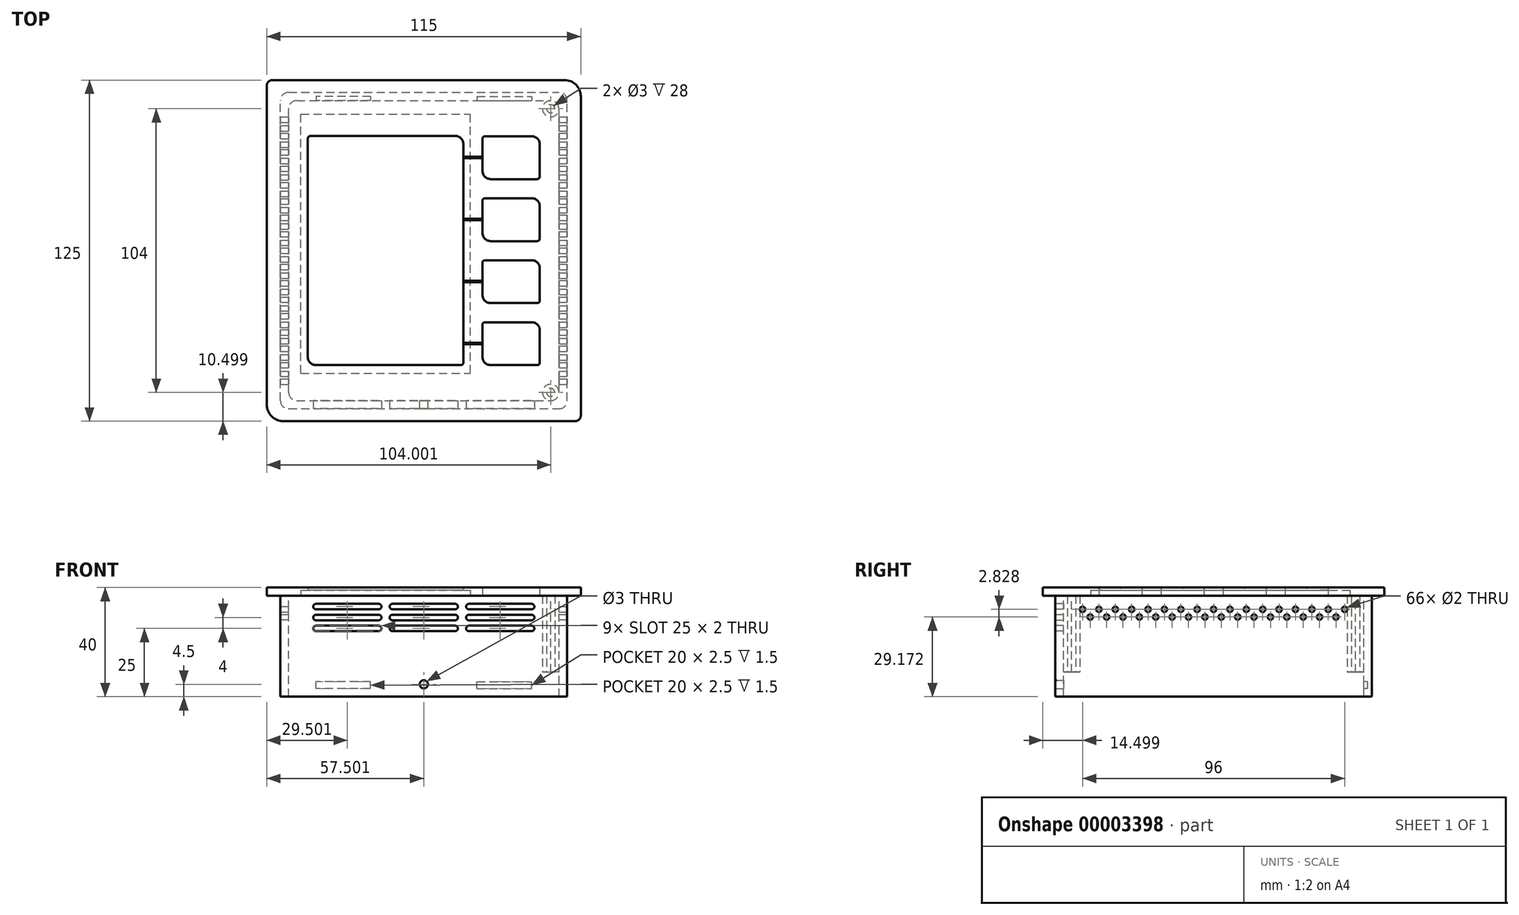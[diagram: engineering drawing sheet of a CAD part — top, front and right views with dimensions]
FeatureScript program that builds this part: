
annotation { "Feature Type Name" : "Feature", "Feature Type Description" : "" }
export const myFeature = defineFeature(function(context is Context, id is Id, definition is map)
    precondition{}
    {
        {
            var Q0;
            Q0=qCreatedBy(makeId("Top.planeOp"),FACE);
            var sketch = newSketch(context, id + "F0", { "sketchPlane" : qUnion([Q0])});
            skLineSegment(sketch, "E0.bottom", {"start": v(-65.66, 62.93) * mm, "end": v(49.34, 62.93) * mm});
            skLineSegment(sketch, "E0.top", {"start": v(-65.66, -62.07) * mm, "end": v(49.34, -62.07) * mm});
            skLineSegment(sketch, "E0.left", {"start": v(-65.66, 62.93) * mm, "end": v(-65.66, -62.07) * mm});
            skLineSegment(sketch, "E0.right", {"start": v(49.34, 62.93) * mm, "end": v(49.34, -62.07) * mm});
            skLineSegment(sketch, "E1.bottom", {"start": v(-50.66, 42.43) * mm, "end": v(6.34, 42.43) * mm});
            skLineSegment(sketch, "E1.top", {"start": v(-50.66, -41.57) * mm, "end": v(6.34, -41.57) * mm});
            skLineSegment(sketch, "E1.left", {"start": v(-50.66, 42.43) * mm, "end": v(-50.66, -41.57) * mm});
            skLineSegment(sketch, "E1.right", {"start": v(6.34, 42.43) * mm, "end": v(6.34, -41.57) * mm});
            skLineSegment(sketch, "E2", {"start": v(13.34, 42.43) * mm, "end": v(13.34, -41.57) * mm, "construction": true});
            skLineSegment(sketch, "E3", {"start": v(34.34, 42.43) * mm, "end": v(34.34, -41.57) * mm, "construction": true});
            skLineSegment(sketch, "E4.bottom", {"start": v(13.34, -41.57) * mm, "end": v(34.34, -41.57) * mm});
            skLineSegment(sketch, "E4.top", {"start": v(13.34, -25.84) * mm, "end": v(34.34, -25.84) * mm});
            skLineSegment(sketch, "E4.left", {"start": v(13.34, -41.57) * mm, "end": v(13.34, -25.84) * mm});
            skLineSegment(sketch, "E4.right", {"start": v(34.34, -41.57) * mm, "end": v(34.34, -25.84) * mm});
            skLineSegment(sketch, "E5.bottom", {"start": v(13.34, -18.84) * mm, "end": v(34.34, -18.84) * mm});
            skLineSegment(sketch, "E5.top", {"start": v(13.34, -3.11) * mm, "end": v(34.34, -3.11) * mm});
            skLineSegment(sketch, "E5.left", {"start": v(13.34, -18.84) * mm, "end": v(13.34, -3.11) * mm});
            skLineSegment(sketch, "E5.right", {"start": v(34.34, -18.84) * mm, "end": v(34.34, -3.11) * mm});
            skLineSegment(sketch, "E6.bottom", {"start": v(13.34, 3.89) * mm, "end": v(34.34, 3.89) * mm});
            skLineSegment(sketch, "E6.top", {"start": v(13.34, 19.62) * mm, "end": v(34.34, 19.62) * mm});
            skLineSegment(sketch, "E6.left", {"start": v(13.34, 3.89) * mm, "end": v(13.34, 19.62) * mm});
            skLineSegment(sketch, "E6.right", {"start": v(34.34, 3.89) * mm, "end": v(34.34, 19.62) * mm});
            skLineSegment(sketch, "E7.bottom", {"start": v(13.34, 26.62) * mm, "end": v(34.34, 26.62) * mm});
            skLineSegment(sketch, "E7.top", {"start": v(13.34, 42.35) * mm, "end": v(34.34, 42.35) * mm});
            skLineSegment(sketch, "E7.left", {"start": v(13.34, 26.62) * mm, "end": v(13.34, 42.35) * mm});
            skLineSegment(sketch, "E7.right", {"start": v(34.34, 26.62) * mm, "end": v(34.34, 42.35) * mm});
            skSolve(sketch);
        }
        {
            var Q0;
            Q0=makeQuery(id+"F0.imprint","IMPRINT",FACE,{"disambiguationData":[TD([[makeQuery(id+"F0.imprint","IMPRINT",EDGE,{"derivedFrom":sQuery(id+"F0.wireOp",EDGE,"E0.bottom")}),-1.0]])]});
            extrude(context, id + "F1", {"entities" : qUnion([Q0]), "depth" : 3 * mm});
        }
        {
            var Q0;
            Q0=makeQuery(id+"F1.opExtrude","SWEPT_EDGE",EDGE,{"disambiguationData":[OSD([sQuery(id+"F0.wireOp",EDGE,"E0.bottom"),sQuery(id+"F0.wireOp",EDGE,"E0.right")])]});
            var Q1;
            Q1=makeQuery(id+"F1.opExtrude","SWEPT_EDGE",EDGE,{"disambiguationData":[OSD([sQuery(id+"F0.wireOp",EDGE,"E0.top"),sQuery(id+"F0.wireOp",EDGE,"E0.left")])]});
            fillet(context, id + "F2", {"entities" : qUnion([Q0, Q1]), "radius" : 6 * mm, "tangentPropagation" : true, "allowEdgeOverflow" : false});
        }
        {
            var Q0;
            Q0=makeQuery(id+"F1.opExtrude","SWEPT_EDGE",EDGE,{"disambiguationData":[OSD([sQuery(id+"F0.wireOp",EDGE,"E7.top"),sQuery(id+"F0.wireOp",EDGE,"E7.right")])]});
            var Q1;
            Q1=makeQuery(id+"F1.opExtrude","SWEPT_EDGE",EDGE,{"disambiguationData":[OSD([sQuery(id+"F0.wireOp",EDGE,"E6.top"),sQuery(id+"F0.wireOp",EDGE,"E6.right")])]});
            var Q2;
            Q2=makeQuery(id+"F1.opExtrude","SWEPT_EDGE",EDGE,{"disambiguationData":[OSD([sQuery(id+"F0.wireOp",EDGE,"E5.top"),sQuery(id+"F0.wireOp",EDGE,"E5.right")])]});
            var Q3;
            Q3=makeQuery(id+"F1.opExtrude","SWEPT_EDGE",EDGE,{"disambiguationData":[OSD([sQuery(id+"F0.wireOp",EDGE,"E4.top"),sQuery(id+"F0.wireOp",EDGE,"E4.right")])]});
            var Q4;
            Q4=makeQuery(id+"F1.opExtrude","SWEPT_EDGE",EDGE,{"disambiguationData":[OSD([sQuery(id+"F0.wireOp",EDGE,"E7.bottom"),sQuery(id+"F0.wireOp",EDGE,"E7.left")])]});
            var Q5;
            Q5=makeQuery(id+"F1.opExtrude","SWEPT_EDGE",EDGE,{"disambiguationData":[OSD([sQuery(id+"F0.wireOp",EDGE,"E6.bottom"),sQuery(id+"F0.wireOp",EDGE,"E6.left")])]});
            var Q6;
            Q6=makeQuery(id+"F1.opExtrude","SWEPT_EDGE",EDGE,{"disambiguationData":[OSD([sQuery(id+"F0.wireOp",EDGE,"E5.bottom"),sQuery(id+"F0.wireOp",EDGE,"E5.left")])]});
            var Q7;
            Q7=makeQuery(id+"F1.opExtrude","SWEPT_EDGE",EDGE,{"disambiguationData":[OSD([sQuery(id+"F0.wireOp",EDGE,"E4.bottom"),sQuery(id+"F0.wireOp",EDGE,"E4.left")])]});
            fillet(context, id + "F3", {"entities" : qUnion([Q0, Q1, Q2, Q3, Q4, Q5, Q6, Q7]), "radius" : 3 * mm, "tangentPropagation" : true, "allowEdgeOverflow" : false});
        }
        {
            var Q0;
            Q0=makeQuery(id+"F1.opExtrude","SWEPT_EDGE",EDGE,{"disambiguationData":[OSD([sQuery(id+"F0.wireOp",EDGE,"E0.bottom"),sQuery(id+"F0.wireOp",EDGE,"E0.left")])]});
            var Q1;
            Q1=makeQuery(id+"F1.opExtrude","SWEPT_EDGE",EDGE,{"disambiguationData":[OSD([sQuery(id+"F0.wireOp",EDGE,"E0.top"),sQuery(id+"F0.wireOp",EDGE,"E0.right")])]});
            fillet(context, id + "F4", {"entities" : qUnion([Q0, Q1]), "radius" : 2 * mm, "tangentPropagation" : true, "allowEdgeOverflow" : false});
        }
        {
            var Q0;
            Q0=makeQuery(id+"F1.opExtrude","SWEPT_EDGE",EDGE,{"disambiguationData":[OSD([sQuery(id+"F0.wireOp",EDGE,"E7.bottom"),sQuery(id+"F0.wireOp",EDGE,"E7.right")])]});
            var Q1;
            Q1=makeQuery(id+"F1.opExtrude","SWEPT_EDGE",EDGE,{"disambiguationData":[OSD([sQuery(id+"F0.wireOp",EDGE,"E6.bottom"),sQuery(id+"F0.wireOp",EDGE,"E6.right")])]});
            var Q2;
            Q2=makeQuery(id+"F1.opExtrude","SWEPT_EDGE",EDGE,{"disambiguationData":[OSD([sQuery(id+"F0.wireOp",EDGE,"E5.bottom"),sQuery(id+"F0.wireOp",EDGE,"E5.right")])]});
            var Q3;
            Q3=makeQuery(id+"F1.opExtrude","SWEPT_EDGE",EDGE,{"disambiguationData":[OSD([sQuery(id+"F0.wireOp",EDGE,"E4.bottom"),sQuery(id+"F0.wireOp",EDGE,"E4.right")])]});
            var Q4;
            Q4=makeQuery(id+"F1.opExtrude","SWEPT_EDGE",EDGE,{"disambiguationData":[OSD([sQuery(id+"F0.wireOp",EDGE,"E4.top"),sQuery(id+"F0.wireOp",EDGE,"E4.left")])]});
            var Q5;
            Q5=makeQuery(id+"F1.opExtrude","SWEPT_EDGE",EDGE,{"disambiguationData":[OSD([sQuery(id+"F0.wireOp",EDGE,"E5.top"),sQuery(id+"F0.wireOp",EDGE,"E5.left")])]});
            var Q6;
            Q6=makeQuery(id+"F1.opExtrude","SWEPT_EDGE",EDGE,{"disambiguationData":[OSD([sQuery(id+"F0.wireOp",EDGE,"E6.top"),sQuery(id+"F0.wireOp",EDGE,"E6.left")])]});
            var Q7;
            Q7=makeQuery(id+"F1.opExtrude","SWEPT_EDGE",EDGE,{"disambiguationData":[OSD([sQuery(id+"F0.wireOp",EDGE,"E7.top"),sQuery(id+"F0.wireOp",EDGE,"E7.left")])]});
            fillet(context, id + "F5", {"entities" : qUnion([Q0, Q1, Q2, Q3, Q4, Q5, Q6, Q7]), "radius" : 1 * mm, "tangentPropagation" : true, "allowEdgeOverflow" : false});
        }
        {
            var Q0;
            Q0=makeQuery(id+"F1.opExtrude","SWEPT_EDGE",EDGE,{"disambiguationData":[OSD([sQuery(id+"F0.wireOp",EDGE,"E1.top"),sQuery(id+"F0.wireOp",EDGE,"E1.right")])]});
            var Q1;
            Q1=makeQuery(id+"F1.opExtrude","SWEPT_EDGE",EDGE,{"disambiguationData":[OSD([sQuery(id+"F0.wireOp",EDGE,"E1.bottom"),sQuery(id+"F0.wireOp",EDGE,"E1.left")])]});
            fillet(context, id + "F6", {"entities" : qUnion([Q0, Q1]), "radius" : 1 * mm, "tangentPropagation" : true, "allowEdgeOverflow" : false});
        }
        {
            var Q0;
            Q0=makeQuery(id+"F1.opExtrude","SWEPT_EDGE",EDGE,{"disambiguationData":[OSD([sQuery(id+"F0.wireOp",EDGE,"E1.bottom"),sQuery(id+"F0.wireOp",EDGE,"E1.right")])]});
            var Q1;
            Q1=makeQuery(id+"F1.opExtrude","SWEPT_EDGE",EDGE,{"disambiguationData":[OSD([sQuery(id+"F0.wireOp",EDGE,"E1.top"),sQuery(id+"F0.wireOp",EDGE,"E1.left")])]});
            fillet(context, id + "F7", {"entities" : qUnion([Q0, Q1]), "radius" : 3 * mm, "tangentPropagation" : true, "allowEdgeOverflow" : false});
        }
        {
            var Q0;
            Q0=makeQuery(id+"F1.opExtrude","CAP_FACE",FACE,{"disambiguationData":[OSD([sQuery(id+"F0.wireOp",EDGE,"E0.bottom"),sQuery(id+"F0.wireOp",EDGE,"E0.top"),sQuery(id+"F0.wireOp",EDGE,"E0.left"),sQuery(id+"F0.wireOp",EDGE,"E0.right"),sQuery(id+"F0.wireOp",EDGE,"E1.bottom"),sQuery(id+"F0.wireOp",EDGE,"E1.top"),sQuery(id+"F0.wireOp",EDGE,"E1.left"),sQuery(id+"F0.wireOp",EDGE,"E1.right"),sQuery(id+"F0.wireOp",EDGE,"E4.bottom"),sQuery(id+"F0.wireOp",EDGE,"E4.top"),sQuery(id+"F0.wireOp",EDGE,"E4.left"),sQuery(id+"F0.wireOp",EDGE,"E4.right"),sQuery(id+"F0.wireOp",EDGE,"E5.bottom"),sQuery(id+"F0.wireOp",EDGE,"E5.top"),sQuery(id+"F0.wireOp",EDGE,"E5.left"),sQuery(id+"F0.wireOp",EDGE,"E5.right"),sQuery(id+"F0.wireOp",EDGE,"E6.bottom"),sQuery(id+"F0.wireOp",EDGE,"E6.top"),sQuery(id+"F0.wireOp",EDGE,"E6.left"),sQuery(id+"F0.wireOp",EDGE,"E6.right"),sQuery(id+"F0.wireOp",EDGE,"E7.bottom"),sQuery(id+"F0.wireOp",EDGE,"E7.top"),sQuery(id+"F0.wireOp",EDGE,"E7.left"),sQuery(id+"F0.wireOp",EDGE,"E7.right")])],"isStart":true});
            var sketch = newSketch(context, id + "F8", { "sketchPlane" : qUnion([Q0])});
            skLineSegment(sketch, "E8.bottom", {"start": v(-60.66, 57.57) * mm, "end": v(44.34, 57.57) * mm});
            skLineSegment(sketch, "E8.top", {"start": v(-60.66, -58.43) * mm, "end": v(44.34, -58.43) * mm});
            skLineSegment(sketch, "E8.left", {"start": v(-60.66, 57.57) * mm, "end": v(-60.66, -58.43) * mm});
            skLineSegment(sketch, "E8.right", {"start": v(44.34, 57.57) * mm, "end": v(44.34, -58.43) * mm});
            skLineSegment(sketch, "E9.0", {"start": v(-57.66, 54.57) * mm, "end": v(41.34, 54.57) * mm});
            skLineSegment(sketch, "E9.1", {"start": v(-57.66, 54.57) * mm, "end": v(-57.66, -55.43) * mm});
            skLineSegment(sketch, "E9.2", {"start": v(-57.66, -55.43) * mm, "end": v(41.34, -55.43) * mm});
            skLineSegment(sketch, "E9.3", {"start": v(41.34, 54.57) * mm, "end": v(41.34, -55.43) * mm});
            skArc(sketch, "E10.0", {"start": v(-70.66, -60.93) * mm, "mid": v(-68.6, -65.88) * mm, "end": v(-63.66, -67.93) * mm});
            skLineSegment(sketch, "E10.1", {"start": v(-63.66, -67.93) * mm, "end": v(43.34, -67.93) * mm});
            skArc(sketch, "E10.2", {"start": v(43.34, -67.93) * mm, "mid": v(51.12, -64.7) * mm, "end": v(54.34, -56.93) * mm});
            skLineSegment(sketch, "E10.3", {"start": v(54.34, -56.93) * mm, "end": v(54.34, 60.07) * mm});
            skArc(sketch, "E10.4", {"start": v(54.34, 60.07) * mm, "mid": v(52.3, 65.02) * mm, "end": v(47.34, 67.07) * mm});
            skLineSegment(sketch, "E10.5", {"start": v(-70.66, -60.93) * mm, "end": v(-70.66, 56.07) * mm});
            skLineSegment(sketch, "E10.6", {"start": v(-59.66, 67.07) * mm, "end": v(47.34, 67.07) * mm});
            skArc(sketch, "E10.7", {"start": v(-59.66, 67.07) * mm, "mid": v(-67.44, 63.85) * mm, "end": v(-70.66, 56.07) * mm});
            skSolve(sketch);
        }
        {
            var Q0;
            Q0=makeQuery(id+"F8.imprint","IMPRINT",FACE,{"disambiguationData":[TD([[makeQuery(id+"F8.imprint","IMPRINT",EDGE,{"derivedFrom":sQuery(id+"F8.wireOp",EDGE,"E8.bottom")}),-1.0]])]});
            extrude(context, id + "F9", {"entities" : qUnion([Q0]), "operationType" : NewBodyOperationType.ADD, "depth" : 37 * mm});
        }
        {
            var Q0;
            Q0=makeQuery(id+"F9.opExtrude","SWEPT_EDGE",EDGE,{"disambiguationData":[OSD([sQuery(id+"F8.wireOp",EDGE,"E8.bottom"),sQuery(id+"F8.wireOp",EDGE,"E8.right")])]});
            var Q1;
            Q1=makeQuery(id+"F9.opExtrude","SWEPT_EDGE",EDGE,{"disambiguationData":[OSD([sQuery(id+"F8.wireOp",EDGE,"E8.top"),sQuery(id+"F8.wireOp",EDGE,"E8.right")])]});
            var Q2;
            Q2=makeQuery(id+"F9.opExtrude","SWEPT_EDGE",EDGE,{"disambiguationData":[OSD([sQuery(id+"F8.wireOp",EDGE,"E8.top"),sQuery(id+"F8.wireOp",EDGE,"E8.left")])]});
            var Q3;
            Q3=makeQuery(id+"F9.opExtrude","SWEPT_EDGE",EDGE,{"disambiguationData":[OSD([sQuery(id+"F8.wireOp",EDGE,"E8.bottom"),sQuery(id+"F8.wireOp",EDGE,"E8.left")])]});
            var Q4;
            Q4=makeQuery(id+"F9.opExtrude","SWEPT_EDGE",EDGE,{"disambiguationData":[OSD([sQuery(id+"F8.wireOp",EDGE,"E9.0"),sQuery(id+"F8.wireOp",EDGE,"E9.1")])]});
            var Q5;
            Q5=makeQuery(id+"F9.opExtrude","SWEPT_EDGE",EDGE,{"disambiguationData":[OSD([sQuery(id+"F8.wireOp",EDGE,"E9.0"),sQuery(id+"F8.wireOp",EDGE,"E9.3")])]});
            var Q6;
            Q6=makeQuery(id+"F9.opExtrude","SWEPT_EDGE",EDGE,{"disambiguationData":[OSD([sQuery(id+"F8.wireOp",EDGE,"E9.1"),sQuery(id+"F8.wireOp",EDGE,"E9.2")])]});
            var Q7;
            Q7=makeQuery(id+"F9.opExtrude","SWEPT_EDGE",EDGE,{"disambiguationData":[OSD([sQuery(id+"F8.wireOp",EDGE,"E9.2"),sQuery(id+"F8.wireOp",EDGE,"E9.3")])]});
            fillet(context, id + "F10", {"entities" : qUnion([Q0, Q1, Q2, Q3, Q4, Q5, Q6, Q7]), "radius" : 3 * mm, "tangentPropagation" : true, "allowEdgeOverflow" : false});
        }
        {
            var Q0;
            Q0=makeQuery(id+"F9.opExtrude","SWEPT_FACE",FACE,{"disambiguationData":[OSD([sQuery(id+"F8.wireOp",EDGE,"E9.2")])]});
            var sketch = newSketch(context, id + "F11", { "sketchPlane" : qUnion([Q0])});
            skLineSegment(sketch, "E11", {"start": v(-8.16, -37) * mm, "end": v(-8.16, 0) * mm, "construction": true});
            skLineSegment(sketch, "E12", {"start": v(-8.16, -34) * mm, "end": v(11.34, -34) * mm, "construction": true});
            skLineSegment(sketch, "E13", {"start": v(-8.16, -34) * mm, "end": v(-27.66, -34) * mm, "construction": true});
            skLineSegment(sketch, "E14.bottom", {"start": v(11.34, -34) * mm, "end": v(31.34, -34) * mm});
            skLineSegment(sketch, "E14.top", {"start": v(11.34, -31.5) * mm, "end": v(31.34, -31.5) * mm});
            skLineSegment(sketch, "E14.left", {"start": v(11.34, -34) * mm, "end": v(11.34, -31.5) * mm});
            skLineSegment(sketch, "E14.right", {"start": v(31.34, -34) * mm, "end": v(31.34, -31.5) * mm});
            skLineSegment(sketch, "E15.0.MirrorCS", {"start": v(-27.66, -34) * mm, "end": v(-27.66, -31.5) * mm});
            skLineSegment(sketch, "E16.0.MirrorCS", {"start": v(-27.66, -34) * mm, "end": v(-47.66, -34) * mm});
            skLineSegment(sketch, "E17.0.MirrorCS", {"start": v(-47.66, -34) * mm, "end": v(-47.66, -31.5) * mm});
            skLineSegment(sketch, "E18.0.MirrorCS", {"start": v(-27.66, -31.5) * mm, "end": v(-47.66, -31.5) * mm});
            skSolve(sketch);
        }
        {
            var Q0;
            Q0=makeQuery(id+"F11.imprint","IMPRINT",FACE,{"disambiguationData":[TD([[makeQuery(id+"F11.imprint","IMPRINT",EDGE,{"derivedFrom":sQuery(id+"F11.wireOp",EDGE,"E15.0.MirrorCS")}),1.0]])]});
            var Q1;
            Q1=makeQuery(id+"F11.imprint","IMPRINT",FACE,{"disambiguationData":[TD([[makeQuery(id+"F11.imprint","IMPRINT",EDGE,{"derivedFrom":sQuery(id+"F11.wireOp",EDGE,"E14.bottom")}),1.0]])]});
            extrude(context, id + "F12", {"entities" : qUnion([Q0, Q1]), "operationType" : NewBodyOperationType.REMOVE, "oppositeDirection" : true, "depth" : 1.5 * mm});
        }
        {
            var Q0;
            Q0=makeQuery(id+"F9.opExtrude","SWEPT_FACE",FACE,{"disambiguationData":[OSD([sQuery(id+"F8.wireOp",EDGE,"E9.0")])]});
            var sketch = newSketch(context, id + "F13", { "sketchPlane" : qUnion([Q0])});
            skLineSegment(sketch, "E19", {"start": v(8.16, -37) * mm, "end": v(8.16, 0) * mm, "construction": true});
            skCircle(sketch, "E20", {"center": v(8.16, -32.5) * mm, "radius": 1.5 * mm});
            skSolve(sketch);
        }
        {
            var Q0;
            Q0=makeQuery(id+"F13.imprint","IMPRINT",FACE,{"disambiguationData":[TD([[makeQuery(id+"F13.imprint","IMPRINT",EDGE,{"derivedFrom":sQuery(id+"F13.wireOp",EDGE,"E20")}),1.0]])]});
            extrude(context, id + "F14", {"entities" : qUnion([Q0]), "operationType" : NewBodyOperationType.REMOVE, "endBound" : BoundingType.THROUGH_ALL, "oppositeDirection" : true, "depth" : 25 * mm});
        }
        {
            var Q0;
            Q0=makeQuery(id+"F14.boolean.opBoolean","INTERSECT",EDGE,{"derivedFrom":[makeQuery(id+"F9.opExtrude","SWEPT_FACE",FACE,{"disambiguationData":[OSD([sQuery(id+"F8.wireOp",EDGE,"E8.bottom")])]}),makeQuery(id+"F14.opExtrude","SWEPT_FACE",FACE,{"disambiguationData":[OSD([sQuery(id+"F13.wireOp",EDGE,"E20")])]})]});
            fillet(context, id + "F15", {"entities" : qUnion([Q0]), "radius" : 0.5 * mm, "tangentPropagation" : true, "allowEdgeOverflow" : false});
        }
        {
            var Q0;
            Q0=makeQuery(id+"F8.imprint","IMPRINT",FACE,{"disambiguationData":[TD([[makeQuery(id+"F8.imprint","IMPRINT",EDGE,{"derivedFrom":sQuery(id+"F8.wireOp",EDGE,"E9.0")}),-1.0]])]});
            cPlane(context, id + "F16", {"entities" : qUnion([Q0]), "cplaneType" : CPlaneType.OFFSET, "offset" : 28 * mm, "width" : 150 * mm, "height" : 150 * mm});
        }
        {
            var Q0;
            Q0=qCreatedBy(id+"F16.planeOp",FACE);
            var sketch = newSketch(context, id + "F17", { "sketchPlane" : qUnion([Q0])});
            skLineSegment(sketch, "E21.bottom", {"start": v(-57.66, 54.62) * mm, "end": v(41.34, 54.62) * mm, "construction": true});
            skLineSegment(sketch, "E21.top", {"start": v(-57.66, -55.38) * mm, "end": v(41.34, -55.38) * mm, "construction": true});
            skLineSegment(sketch, "E21.left", {"start": v(-57.66, 54.62) * mm, "end": v(-57.66, -55.38) * mm, "construction": true});
            skLineSegment(sketch, "E21.right", {"start": v(41.34, 54.62) * mm, "end": v(41.34, -55.38) * mm, "construction": true});
            skLineSegment(sketch, "E22", {"start": v(-8.16, 54.62) * mm, "end": v(-8.16, -55.38) * mm, "construction": true});
            skLineSegment(sketch, "E23", {"start": v(-57.66, -0.38) * mm, "end": v(41.34, -0.38) * mm, "construction": true});
            skCircle(sketch, "E24.2.MirrorC", {"center": v(-54.66, 51.62) * mm, "radius": 3 * mm});
            skCircle(sketch, "E24.3.MirrorC", {"center": v(-54.66, 51.62) * mm, "radius": 1.5 * mm});
            skCircle(sketch, "E25", {"center": v(38.34, -52.43) * mm, "radius": 3 * mm});
            skCircle(sketch, "E26", {"center": v(38.34, -52.43) * mm, "radius": 1.5 * mm});
            skCircle(sketch, "E27", {"center": v(38.34, 51.57) * mm, "radius": 3 * mm});
            skCircle(sketch, "E28", {"center": v(38.34, 51.57) * mm, "radius": 1.5 * mm});
            skSolve(sketch);
        }
        {
            var Q0;
            Q0=makeQuery(id+"F17.imprint","IMPRINT",FACE,{"disambiguationData":[TD([[makeQuery(id+"F17.imprint","IMPRINT",EDGE,{"derivedFrom":sQuery(id+"F17.wireOp",EDGE,"E24.2.MirrorC")}),-1.0]])]});
            var Q1;
            Q1=makeQuery(id+"F17.imprint","IMPRINT",FACE,{"disambiguationData":[TD([[makeQuery(id+"F17.imprint","IMPRINT",EDGE,{"derivedFrom":sQuery(id+"F17.wireOp",EDGE,"E27")}),1.0]])]});
            var Q2;
            Q2=makeQuery(id+"F17.imprint","IMPRINT",FACE,{"disambiguationData":[TD([[makeQuery(id+"F17.imprint","IMPRINT",EDGE,{"derivedFrom":sQuery(id+"F17.wireOp",EDGE,"E25")}),1.0]])]});
            extrude(context, id + "F18", {"entities" : qUnion([Q0, Q1, Q2]), "operationType" : NewBodyOperationType.ADD, "endBound" : BoundingType.UP_TO_NEXT, "oppositeDirection" : true, "depth" : 26.41 * mm});
        }
        {
            var Q0;
            Q0=makeQuery(id+"F8.imprint","IMPRINT",FACE,{"disambiguationData":[TD([[makeQuery(id+"F8.imprint","IMPRINT",EDGE,{"derivedFrom":sQuery(id+"F8.wireOp",EDGE,"E9.0")}),-1.0]])]});
            var sketch = newSketch(context, id + "F19", { "sketchPlane" : qUnion([Q0])});
            skLineSegment(sketch, "E29.bottom", {"start": v(-53.16, 44.57) * mm, "end": v(8.84, 44.57) * mm});
            skLineSegment(sketch, "E29.top", {"start": v(-53.16, -50.43) * mm, "end": v(8.84, -50.43) * mm});
            skLineSegment(sketch, "E29.left", {"start": v(-53.16, 44.57) * mm, "end": v(-53.16, -50.43) * mm});
            skLineSegment(sketch, "E29.right", {"start": v(8.84, 44.57) * mm, "end": v(8.84, -50.43) * mm});
            skSolve(sketch);
        }
        {
            var Q0;
            {var subQ6=sQuery(id+"F0.wireOp",EDGE,"E1.top");var subQ7=makeQuery(id+"F19.imprint","IMPRINT",EDGE,{"derivedFrom":makeQuery(id+"F8.imprint","IMPRINT",EDGE,{"derivedFrom":makeQuery(id+"F1.opExtrude","CAP_EDGE",EDGE,{"disambiguationData":[OSD([subQ6])],"isStart":true})})});Q0=qUnion([makeQuery(id+"F19.imprint","IMPRINT",FACE,{"disambiguationData":[TD([[subQ7,-1.0]])]}),makeQuery(id+"F19.imprint","IMPRINT",FACE,{"disambiguationData":[TD([[makeQuery(id+"F19.imprint","IMPRINT",EDGE,{"derivedFrom":sQuery(id+"F19.wireOp",EDGE,"E29.bottom")}),-1.0]])]})]);}
            extrude(context, id + "F20", {"entities" : qUnion([Q0]), "operationType" : NewBodyOperationType.REMOVE, "oppositeDirection" : true, "depth" : 2 * mm});
        }
        {
            var Q0;
            Q0=makeQuery(id+"F9.opExtrude","SWEPT_FACE",FACE,{"disambiguationData":[OSD([sQuery(id+"F8.wireOp",EDGE,"E8.bottom")])]});
            var sketch = newSketch(context, id + "F21", { "sketchPlane" : qUnion([Q0])});
            skSolve(sketch);
        }
        {
            var Q0;
            {var subQ0=sQuery(id+"F8.wireOp",EDGE,"E8.bottom");Q0=makeQuery(id+"F21.imprint","IMPRINT",FACE,{"disambiguationData":[TD([[makeQuery(id+"F21.imprint","IMPRINT",EDGE,{"derivedFrom":makeQuery(id+"F9.opExtrude","CAP_EDGE",EDGE,{"disambiguationData":[OSD([subQ0])],"isStart":false})}),1.0]])]});}
            var sketch = newSketch(context, id + "F22", { "sketchPlane" : qUnion([Q0])});
            skLineSegment(sketch, "E30.bottom", {"start": v(-24.66, -3) * mm, "end": v(-47.66, -3) * mm});
            skLineSegment(sketch, "E30.top", {"start": v(-24.66, -5) * mm, "end": v(-47.66, -5) * mm});
            skLineSegment(sketch, "E30.left", {"start": v(-23.66, -4) * mm, "end": v(-23.66, -4) * mm});
            skLineSegment(sketch, "E30.right", {"start": v(-48.66, -4) * mm, "end": v(-48.66, -4) * mm});
            skLineSegment(sketch, "E31.direction1", {"start": v(-48.66, -3) * mm, "end": v(32.34, -3) * mm, "construction": true});
            skLineSegment(sketch, "E31.direction2", {"start": v(-48.66, -3) * mm, "end": v(-48.66, -6.5) * mm, "construction": true});
            skPoint(sketch, "E32.visualSharp", {"position": v(-48.66, -5) * mm});
            skArc(sketch, "E32.filletArc", {"start": v(-48.66, -4) * mm, "mid": v(-48.37, -4.7) * mm, "end": v(-47.66, -5) * mm});
            skPoint(sketch, "E33.visualSharp", {"position": v(-48.66, -3) * mm});
            skArc(sketch, "E33.filletArc", {"start": v(-47.66, -3) * mm, "mid": v(-48.37, -3.3) * mm, "end": v(-48.66, -4) * mm});
            skPoint(sketch, "E34.visualSharp", {"position": v(-23.66, -3) * mm});
            skArc(sketch, "E34.filletArc", {"start": v(-23.66, -4) * mm, "mid": v(-23.95, -3.3) * mm, "end": v(-24.66, -3) * mm});
            skPoint(sketch, "E35.visualSharp", {"position": v(-23.66, -5) * mm});
            skArc(sketch, "E35.filletArc", {"start": v(-24.66, -5) * mm, "mid": v(-23.95, -4.7) * mm, "end": v(-23.66, -4) * mm});
            skArc(sketch, "E36.0.1.0", {"start": v(-23.66, -8) * mm, "mid": v(-23.95, -7.3) * mm, "end": v(-24.66, -7) * mm});
            skPoint(sketch, "E36.0.1.1", {"position": v(-23.66, -9) * mm});
            skArc(sketch, "E36.0.1.2", {"start": v(-24.66, -9) * mm, "mid": v(-23.95, -8.7) * mm, "end": v(-23.66, -8) * mm});
            skArc(sketch, "E36.0.1.3", {"start": v(-48.66, -8) * mm, "mid": v(-48.37, -8.7) * mm, "end": v(-47.66, -9) * mm});
            skLineSegment(sketch, "E36.0.1.4", {"start": v(-24.66, -9) * mm, "end": v(-47.66, -9) * mm});
            skLineSegment(sketch, "E36.0.1.5", {"start": v(-24.66, -7) * mm, "end": v(-47.66, -7) * mm});
            skPoint(sketch, "E36.0.1.6", {"position": v(-23.66, -7) * mm});
            skPoint(sketch, "E36.0.1.7", {"position": v(-48.66, -7) * mm});
            skArc(sketch, "E36.0.1.8", {"start": v(-47.66, -7) * mm, "mid": v(-48.37, -7.3) * mm, "end": v(-48.66, -8) * mm});
            skPoint(sketch, "E36.0.1.9", {"position": v(-48.66, -9) * mm});
            skArc(sketch, "E36.0.2.0", {"start": v(-23.66, -12) * mm, "mid": v(-23.95, -11.3) * mm, "end": v(-24.66, -11) * mm});
            skPoint(sketch, "E36.0.2.1", {"position": v(-23.66, -13) * mm});
            skArc(sketch, "E36.0.2.2", {"start": v(-24.66, -13) * mm, "mid": v(-23.95, -12.7) * mm, "end": v(-23.66, -12) * mm});
            skArc(sketch, "E36.0.2.3", {"start": v(-48.66, -12) * mm, "mid": v(-48.37, -12.7) * mm, "end": v(-47.66, -13) * mm});
            skLineSegment(sketch, "E36.0.2.4", {"start": v(-24.66, -13) * mm, "end": v(-47.66, -13) * mm});
            skLineSegment(sketch, "E36.0.2.5", {"start": v(-24.66, -11) * mm, "end": v(-47.66, -11) * mm});
            skPoint(sketch, "E36.0.2.6", {"position": v(-23.66, -11) * mm});
            skPoint(sketch, "E36.0.2.7", {"position": v(-48.66, -11) * mm});
            skArc(sketch, "E36.0.2.8", {"start": v(-47.66, -11) * mm, "mid": v(-48.37, -11.3) * mm, "end": v(-48.66, -12) * mm});
            skPoint(sketch, "E36.0.2.9", {"position": v(-48.66, -13) * mm});
            skArc(sketch, "E36.1.0.0", {"start": v(4.34, -4) * mm, "mid": v(4.05, -3.3) * mm, "end": v(3.34, -3) * mm});
            skPoint(sketch, "E36.1.0.1", {"position": v(4.34, -5) * mm});
            skArc(sketch, "E36.1.0.2", {"start": v(3.34, -5) * mm, "mid": v(4.05, -4.7) * mm, "end": v(4.34, -4) * mm});
            skArc(sketch, "E36.1.0.3", {"start": v(-20.66, -4) * mm, "mid": v(-20.37, -4.7) * mm, "end": v(-19.66, -5) * mm});
            skLineSegment(sketch, "E36.1.0.4", {"start": v(3.34, -5) * mm, "end": v(-19.66, -5) * mm});
            skLineSegment(sketch, "E36.1.0.5", {"start": v(3.34, -3) * mm, "end": v(-19.66, -3) * mm});
            skPoint(sketch, "E36.1.0.6", {"position": v(4.34, -3) * mm});
            skPoint(sketch, "E36.1.0.7", {"position": v(-20.66, -3) * mm});
            skArc(sketch, "E36.1.0.8", {"start": v(-19.66, -3) * mm, "mid": v(-20.37, -3.3) * mm, "end": v(-20.66, -4) * mm});
            skPoint(sketch, "E36.1.0.9", {"position": v(-20.66, -5) * mm});
            skArc(sketch, "E36.1.1.0", {"start": v(4.34, -8) * mm, "mid": v(4.05, -7.3) * mm, "end": v(3.34, -7) * mm});
            skPoint(sketch, "E36.1.1.1", {"position": v(4.34, -9) * mm});
            skArc(sketch, "E36.1.1.2", {"start": v(3.34, -9) * mm, "mid": v(4.05, -8.7) * mm, "end": v(4.34, -8) * mm});
            skArc(sketch, "E36.1.1.3", {"start": v(-20.66, -8) * mm, "mid": v(-20.37, -8.7) * mm, "end": v(-19.66, -9) * mm});
            skLineSegment(sketch, "E36.1.1.4", {"start": v(3.34, -9) * mm, "end": v(-19.66, -9) * mm});
            skLineSegment(sketch, "E36.1.1.5", {"start": v(3.34, -7) * mm, "end": v(-19.66, -7) * mm});
            skPoint(sketch, "E36.1.1.6", {"position": v(4.34, -7) * mm});
            skPoint(sketch, "E36.1.1.7", {"position": v(-20.66, -7) * mm});
            skArc(sketch, "E36.1.1.8", {"start": v(-19.66, -7) * mm, "mid": v(-20.37, -7.3) * mm, "end": v(-20.66, -8) * mm});
            skPoint(sketch, "E36.1.1.9", {"position": v(-20.66, -9) * mm});
            skArc(sketch, "E36.1.2.0", {"start": v(4.34, -12) * mm, "mid": v(4.05, -11.3) * mm, "end": v(3.34, -11) * mm});
            skPoint(sketch, "E36.1.2.1", {"position": v(4.34, -13) * mm});
            skArc(sketch, "E36.1.2.2", {"start": v(3.34, -13) * mm, "mid": v(4.05, -12.7) * mm, "end": v(4.34, -12) * mm});
            skArc(sketch, "E36.1.2.3", {"start": v(-20.66, -12) * mm, "mid": v(-20.37, -12.7) * mm, "end": v(-19.66, -13) * mm});
            skLineSegment(sketch, "E36.1.2.4", {"start": v(3.34, -13) * mm, "end": v(-19.66, -13) * mm});
            skLineSegment(sketch, "E36.1.2.5", {"start": v(3.34, -11) * mm, "end": v(-19.66, -11) * mm});
            skPoint(sketch, "E36.1.2.6", {"position": v(4.34, -11) * mm});
            skPoint(sketch, "E36.1.2.7", {"position": v(-20.66, -11) * mm});
            skArc(sketch, "E36.1.2.8", {"start": v(-19.66, -11) * mm, "mid": v(-20.37, -11.3) * mm, "end": v(-20.66, -12) * mm});
            skPoint(sketch, "E36.1.2.9", {"position": v(-20.66, -13) * mm});
            skArc(sketch, "E36.2.0.0", {"start": v(32.34, -4) * mm, "mid": v(32.05, -3.3) * mm, "end": v(31.34, -3) * mm});
            skPoint(sketch, "E36.2.0.1", {"position": v(32.34, -5) * mm});
            skArc(sketch, "E36.2.0.2", {"start": v(31.34, -5) * mm, "mid": v(32.05, -4.7) * mm, "end": v(32.34, -4) * mm});
            skArc(sketch, "E36.2.0.3", {"start": v(7.34, -4) * mm, "mid": v(7.63, -4.7) * mm, "end": v(8.34, -5) * mm});
            skLineSegment(sketch, "E36.2.0.4", {"start": v(31.34, -5) * mm, "end": v(8.34, -5) * mm});
            skLineSegment(sketch, "E36.2.0.5", {"start": v(31.34, -3) * mm, "end": v(8.34, -3) * mm});
            skPoint(sketch, "E36.2.0.6", {"position": v(32.34, -3) * mm});
            skPoint(sketch, "E36.2.0.7", {"position": v(7.34, -3) * mm});
            skArc(sketch, "E36.2.0.8", {"start": v(8.34, -3) * mm, "mid": v(7.63, -3.3) * mm, "end": v(7.34, -4) * mm});
            skPoint(sketch, "E36.2.0.9", {"position": v(7.34, -5) * mm});
            skArc(sketch, "E36.2.1.0", {"start": v(32.34, -8) * mm, "mid": v(32.05, -7.3) * mm, "end": v(31.34, -7) * mm});
            skPoint(sketch, "E36.2.1.1", {"position": v(32.34, -9) * mm});
            skArc(sketch, "E36.2.1.2", {"start": v(31.34, -9) * mm, "mid": v(32.05, -8.7) * mm, "end": v(32.34, -8) * mm});
            skArc(sketch, "E36.2.1.3", {"start": v(7.34, -8) * mm, "mid": v(7.63, -8.7) * mm, "end": v(8.34, -9) * mm});
            skLineSegment(sketch, "E36.2.1.4", {"start": v(31.34, -9) * mm, "end": v(8.34, -9) * mm});
            skLineSegment(sketch, "E36.2.1.5", {"start": v(31.34, -7) * mm, "end": v(8.34, -7) * mm});
            skPoint(sketch, "E36.2.1.6", {"position": v(32.34, -7) * mm});
            skPoint(sketch, "E36.2.1.7", {"position": v(7.34, -7) * mm});
            skArc(sketch, "E36.2.1.8", {"start": v(8.34, -7) * mm, "mid": v(7.63, -7.3) * mm, "end": v(7.34, -8) * mm});
            skPoint(sketch, "E36.2.1.9", {"position": v(7.34, -9) * mm});
            skArc(sketch, "E36.2.2.0", {"start": v(32.34, -12) * mm, "mid": v(32.05, -11.3) * mm, "end": v(31.34, -11) * mm});
            skPoint(sketch, "E36.2.2.1", {"position": v(32.34, -13) * mm});
            skArc(sketch, "E36.2.2.2", {"start": v(31.34, -13) * mm, "mid": v(32.05, -12.7) * mm, "end": v(32.34, -12) * mm});
            skArc(sketch, "E36.2.2.3", {"start": v(7.34, -12) * mm, "mid": v(7.63, -12.7) * mm, "end": v(8.34, -13) * mm});
            skLineSegment(sketch, "E36.2.2.4", {"start": v(31.34, -13) * mm, "end": v(8.34, -13) * mm});
            skLineSegment(sketch, "E36.2.2.5", {"start": v(31.34, -11) * mm, "end": v(8.34, -11) * mm});
            skPoint(sketch, "E36.2.2.6", {"position": v(32.34, -11) * mm});
            skPoint(sketch, "E36.2.2.7", {"position": v(7.34, -11) * mm});
            skArc(sketch, "E36.2.2.8", {"start": v(8.34, -11) * mm, "mid": v(7.63, -11.3) * mm, "end": v(7.34, -12) * mm});
            skPoint(sketch, "E36.2.2.9", {"position": v(7.34, -13) * mm});
            skLineSegment(sketch, "E36.direction1", {"start": v(-24.66, -4) * mm, "end": v(3.34, -4) * mm, "construction": true});
            skLineSegment(sketch, "E36.direction2", {"start": v(-24.66, -4) * mm, "end": v(-24.66, -8) * mm, "construction": true});
            skSolve(sketch);
        }
        {
            var Q0;
            Q0=makeQuery(id+"F22.imprint","IMPRINT",FACE,{"disambiguationData":[TD([[makeQuery(id+"F22.imprint","IMPRINT",EDGE,{"derivedFrom":sQuery(id+"F22.wireOp",EDGE,"E31.0.1.0")}),1.0]])]});
            var Q1;
            Q1=makeQuery(id+"F22.imprint","IMPRINT",FACE,{"disambiguationData":[TD([[makeQuery(id+"F22.imprint","IMPRINT",EDGE,{"derivedFrom":sQuery(id+"F22.wireOp",EDGE,"E30.bottom")}),1.0]])]});
            var Q2;
            Q2=makeQuery(id+"F22.imprint","IMPRINT",FACE,{"disambiguationData":[TD([[makeQuery(id+"F22.imprint","IMPRINT",EDGE,{"derivedFrom":sQuery(id+"F22.wireOp",EDGE,"E31.0.2.0")}),1.0]])]});
            extrude(context, id + "F23", {"entities" : qUnion([Q0, Q1, Q2]), "operationType" : NewBodyOperationType.REMOVE, "oppositeDirection" : true, "depth" : 4 * mm});
        }
        {
            var Q0;
            Q0=makeQuery(id+"F9.opExtrude","SWEPT_FACE",FACE,{"disambiguationData":[OSD([sQuery(id+"F8.wireOp",EDGE,"E8.right")])]});
            var sketch = newSketch(context, id + "F24", { "sketchPlane" : qUnion([Q0])});
            skCircle(sketch, "E37", {"center": v(-47.57, -5) * mm, "radius": 1 * mm});
            skCircle(sketch, "E38", {"center": v(-44.74, -7.83) * mm, "radius": 1 * mm});
            skCircle(sketch, "E39.1.0.0", {"center": v(-41.57, -5) * mm, "radius": 1 * mm});
            skCircle(sketch, "E39.1.0.1", {"center": v(-38.74, -7.83) * mm, "radius": 1 * mm});
            skCircle(sketch, "E39.2.0.0", {"center": v(-35.57, -5) * mm, "radius": 1 * mm});
            skCircle(sketch, "E39.2.0.1", {"center": v(-32.74, -7.83) * mm, "radius": 1 * mm});
            skCircle(sketch, "E39.3.0.0", {"center": v(-29.57, -5) * mm, "radius": 1 * mm});
            skCircle(sketch, "E39.3.0.1", {"center": v(-26.74, -7.83) * mm, "radius": 1 * mm});
            skCircle(sketch, "E39.4.0.0", {"center": v(-23.57, -5) * mm, "radius": 1 * mm});
            skCircle(sketch, "E39.4.0.1", {"center": v(-20.74, -7.83) * mm, "radius": 1 * mm});
            skCircle(sketch, "E39.5.0.0", {"center": v(-17.57, -5) * mm, "radius": 1 * mm});
            skCircle(sketch, "E39.5.0.1", {"center": v(-14.74, -7.83) * mm, "radius": 1 * mm});
            skCircle(sketch, "E39.6.0.0", {"center": v(-11.57, -5) * mm, "radius": 1 * mm});
            skCircle(sketch, "E39.6.0.1", {"center": v(-8.74, -7.83) * mm, "radius": 1 * mm});
            skCircle(sketch, "E39.7.0.0", {"center": v(-5.57, -5) * mm, "radius": 1 * mm});
            skCircle(sketch, "E39.7.0.1", {"center": v(-2.74, -7.83) * mm, "radius": 1 * mm});
            skCircle(sketch, "E39.8.0.0", {"center": v(0.43, -5) * mm, "radius": 1 * mm});
            skCircle(sketch, "E39.8.0.1", {"center": v(3.26, -7.83) * mm, "radius": 1 * mm});
            skCircle(sketch, "E39.9.0.0", {"center": v(6.43, -5) * mm, "radius": 1 * mm});
            skCircle(sketch, "E39.9.0.1", {"center": v(9.26, -7.83) * mm, "radius": 1 * mm});
            skCircle(sketch, "E39.10.0.0", {"center": v(12.43, -5) * mm, "radius": 1 * mm});
            skCircle(sketch, "E39.10.0.1", {"center": v(15.26, -7.83) * mm, "radius": 1 * mm});
            skCircle(sketch, "E39.11.0.0", {"center": v(18.43, -5) * mm, "radius": 1 * mm});
            skCircle(sketch, "E39.11.0.1", {"center": v(21.26, -7.83) * mm, "radius": 1 * mm});
            skCircle(sketch, "E39.12.0.0", {"center": v(24.43, -5) * mm, "radius": 1 * mm});
            skCircle(sketch, "E39.12.0.1", {"center": v(27.26, -7.83) * mm, "radius": 1 * mm});
            skCircle(sketch, "E39.13.0.0", {"center": v(30.43, -5) * mm, "radius": 1 * mm});
            skCircle(sketch, "E39.13.0.1", {"center": v(33.26, -7.83) * mm, "radius": 1 * mm});
            skCircle(sketch, "E39.14.0.0", {"center": v(36.43, -5) * mm, "radius": 1 * mm});
            skCircle(sketch, "E39.14.0.1", {"center": v(39.26, -7.83) * mm, "radius": 1 * mm});
            skCircle(sketch, "E39.15.0.0", {"center": v(42.43, -5) * mm, "radius": 1 * mm});
            skCircle(sketch, "E39.15.0.1", {"center": v(45.26, -7.83) * mm, "radius": 1 * mm});
            skCircle(sketch, "E39.16.0.0", {"center": v(48.43, -5) * mm, "radius": 1 * mm});
            skLineSegment(sketch, "E39.direction1", {"start": v(-47.57, -5) * mm, "end": v(-41.57, -5) * mm, "construction": true});
            skSolve(sketch);
        }
        {
            var Q0;
            {Q0=qUnion([makeQuery(id+"F24.imprint","IMPRINT",FACE,{"disambiguationData":[TD([[makeQuery(id+"F24.imprint","IMPRINT",EDGE,{"derivedFrom":sQuery(id+"F24.wireOp",EDGE,"E37")}),1.0]])]}),makeQuery(id+"F24.imprint","IMPRINT",FACE,{"disambiguationData":[TD([[makeQuery(id+"F24.imprint","IMPRINT",EDGE,{"derivedFrom":sQuery(id+"F24.wireOp",EDGE,"E38")}),1.0]])]}),makeQuery(id+"F24.imprint","IMPRINT",FACE,{"disambiguationData":[TD([[makeQuery(id+"F24.imprint","IMPRINT",EDGE,{"derivedFrom":sQuery(id+"F24.wireOp",EDGE,"E39.1.0.0")}),1.0]])]}),makeQuery(id+"F24.imprint","IMPRINT",FACE,{"disambiguationData":[TD([[makeQuery(id+"F24.imprint","IMPRINT",EDGE,{"derivedFrom":sQuery(id+"F24.wireOp",EDGE,"E39.1.0.1")}),1.0]])]}),makeQuery(id+"F24.imprint","IMPRINT",FACE,{"disambiguationData":[TD([[makeQuery(id+"F24.imprint","IMPRINT",EDGE,{"derivedFrom":sQuery(id+"F24.wireOp",EDGE,"E39.2.0.0")}),1.0]])]}),makeQuery(id+"F24.imprint","IMPRINT",FACE,{"disambiguationData":[TD([[makeQuery(id+"F24.imprint","IMPRINT",EDGE,{"derivedFrom":sQuery(id+"F24.wireOp",EDGE,"E39.2.0.1")}),1.0]])]}),makeQuery(id+"F24.imprint","IMPRINT",FACE,{"disambiguationData":[TD([[makeQuery(id+"F24.imprint","IMPRINT",EDGE,{"derivedFrom":sQuery(id+"F24.wireOp",EDGE,"E39.3.0.0")}),1.0]])]}),makeQuery(id+"F24.imprint","IMPRINT",FACE,{"disambiguationData":[TD([[makeQuery(id+"F24.imprint","IMPRINT",EDGE,{"derivedFrom":sQuery(id+"F24.wireOp",EDGE,"E39.3.0.1")}),1.0]])]}),makeQuery(id+"F24.imprint","IMPRINT",FACE,{"disambiguationData":[TD([[makeQuery(id+"F24.imprint","IMPRINT",EDGE,{"derivedFrom":sQuery(id+"F24.wireOp",EDGE,"E39.4.0.0")}),1.0]])]}),makeQuery(id+"F24.imprint","IMPRINT",FACE,{"disambiguationData":[TD([[makeQuery(id+"F24.imprint","IMPRINT",EDGE,{"derivedFrom":sQuery(id+"F24.wireOp",EDGE,"E39.4.0.1")}),1.0]])]}),makeQuery(id+"F24.imprint","IMPRINT",FACE,{"disambiguationData":[TD([[makeQuery(id+"F24.imprint","IMPRINT",EDGE,{"derivedFrom":sQuery(id+"F24.wireOp",EDGE,"E39.5.0.0")}),1.0]])]}),makeQuery(id+"F24.imprint","IMPRINT",FACE,{"disambiguationData":[TD([[makeQuery(id+"F24.imprint","IMPRINT",EDGE,{"derivedFrom":sQuery(id+"F24.wireOp",EDGE,"E39.5.0.1")}),1.0]])]}),makeQuery(id+"F24.imprint","IMPRINT",FACE,{"disambiguationData":[TD([[makeQuery(id+"F24.imprint","IMPRINT",EDGE,{"derivedFrom":sQuery(id+"F24.wireOp",EDGE,"E39.6.0.0")}),1.0]])]}),makeQuery(id+"F24.imprint","IMPRINT",FACE,{"disambiguationData":[TD([[makeQuery(id+"F24.imprint","IMPRINT",EDGE,{"derivedFrom":sQuery(id+"F24.wireOp",EDGE,"E39.6.0.1")}),1.0]])]}),makeQuery(id+"F24.imprint","IMPRINT",FACE,{"disambiguationData":[TD([[makeQuery(id+"F24.imprint","IMPRINT",EDGE,{"derivedFrom":sQuery(id+"F24.wireOp",EDGE,"E39.7.0.0")}),1.0]])]}),makeQuery(id+"F24.imprint","IMPRINT",FACE,{"disambiguationData":[TD([[makeQuery(id+"F24.imprint","IMPRINT",EDGE,{"derivedFrom":sQuery(id+"F24.wireOp",EDGE,"E39.7.0.1")}),1.0]])]}),makeQuery(id+"F24.imprint","IMPRINT",FACE,{"disambiguationData":[TD([[makeQuery(id+"F24.imprint","IMPRINT",EDGE,{"derivedFrom":sQuery(id+"F24.wireOp",EDGE,"E39.8.0.0")}),1.0]])]}),makeQuery(id+"F24.imprint","IMPRINT",FACE,{"disambiguationData":[TD([[makeQuery(id+"F24.imprint","IMPRINT",EDGE,{"derivedFrom":sQuery(id+"F24.wireOp",EDGE,"E39.8.0.1")}),1.0]])]}),makeQuery(id+"F24.imprint","IMPRINT",FACE,{"disambiguationData":[TD([[makeQuery(id+"F24.imprint","IMPRINT",EDGE,{"derivedFrom":sQuery(id+"F24.wireOp",EDGE,"E39.9.0.0")}),1.0]])]}),makeQuery(id+"F24.imprint","IMPRINT",FACE,{"disambiguationData":[TD([[makeQuery(id+"F24.imprint","IMPRINT",EDGE,{"derivedFrom":sQuery(id+"F24.wireOp",EDGE,"E39.9.0.1")}),1.0]])]}),makeQuery(id+"F24.imprint","IMPRINT",FACE,{"disambiguationData":[TD([[makeQuery(id+"F24.imprint","IMPRINT",EDGE,{"derivedFrom":sQuery(id+"F24.wireOp",EDGE,"E39.10.0.0")}),1.0]])]}),makeQuery(id+"F24.imprint","IMPRINT",FACE,{"disambiguationData":[TD([[makeQuery(id+"F24.imprint","IMPRINT",EDGE,{"derivedFrom":sQuery(id+"F24.wireOp",EDGE,"E39.10.0.1")}),1.0]])]}),makeQuery(id+"F24.imprint","IMPRINT",FACE,{"disambiguationData":[TD([[makeQuery(id+"F24.imprint","IMPRINT",EDGE,{"derivedFrom":sQuery(id+"F24.wireOp",EDGE,"E39.11.0.0")}),1.0]])]}),makeQuery(id+"F24.imprint","IMPRINT",FACE,{"disambiguationData":[TD([[makeQuery(id+"F24.imprint","IMPRINT",EDGE,{"derivedFrom":sQuery(id+"F24.wireOp",EDGE,"E39.11.0.1")}),1.0]])]}),makeQuery(id+"F24.imprint","IMPRINT",FACE,{"disambiguationData":[TD([[makeQuery(id+"F24.imprint","IMPRINT",EDGE,{"derivedFrom":sQuery(id+"F24.wireOp",EDGE,"E39.12.0.0")}),1.0]])]}),makeQuery(id+"F24.imprint","IMPRINT",FACE,{"disambiguationData":[TD([[makeQuery(id+"F24.imprint","IMPRINT",EDGE,{"derivedFrom":sQuery(id+"F24.wireOp",EDGE,"E39.12.0.1")}),1.0]])]}),makeQuery(id+"F24.imprint","IMPRINT",FACE,{"disambiguationData":[TD([[makeQuery(id+"F24.imprint","IMPRINT",EDGE,{"derivedFrom":sQuery(id+"F24.wireOp",EDGE,"E39.13.0.0")}),1.0]])]}),makeQuery(id+"F24.imprint","IMPRINT",FACE,{"disambiguationData":[TD([[makeQuery(id+"F24.imprint","IMPRINT",EDGE,{"derivedFrom":sQuery(id+"F24.wireOp",EDGE,"E39.13.0.1")}),1.0]])]}),makeQuery(id+"F24.imprint","IMPRINT",FACE,{"disambiguationData":[TD([[makeQuery(id+"F24.imprint","IMPRINT",EDGE,{"derivedFrom":sQuery(id+"F24.wireOp",EDGE,"E39.14.0.0")}),1.0]])]}),makeQuery(id+"F24.imprint","IMPRINT",FACE,{"disambiguationData":[TD([[makeQuery(id+"F24.imprint","IMPRINT",EDGE,{"derivedFrom":sQuery(id+"F24.wireOp",EDGE,"E39.14.0.1")}),1.0]])]}),makeQuery(id+"F24.imprint","IMPRINT",FACE,{"disambiguationData":[TD([[makeQuery(id+"F24.imprint","IMPRINT",EDGE,{"derivedFrom":sQuery(id+"F24.wireOp",EDGE,"E39.15.0.0")}),1.0]])]}),makeQuery(id+"F24.imprint","IMPRINT",FACE,{"disambiguationData":[TD([[makeQuery(id+"F24.imprint","IMPRINT",EDGE,{"derivedFrom":sQuery(id+"F24.wireOp",EDGE,"E39.15.0.1")}),1.0]])]}),makeQuery(id+"F24.imprint","IMPRINT",FACE,{"disambiguationData":[TD([[makeQuery(id+"F24.imprint","IMPRINT",EDGE,{"derivedFrom":sQuery(id+"F24.wireOp",EDGE,"E39.16.0.0")}),1.0]])]})]);}
            extrude(context, id + "F25", {"entities" : qUnion([Q0]), "operationType" : NewBodyOperationType.REMOVE, "endBound" : BoundingType.THROUGH_ALL, "oppositeDirection" : true, "depth" : 25 * mm});
        }
        {
            var Q0;
            Q0=makeQuery(id+"F1.opExtrude","SWEPT_FACE",FACE,{"disambiguationData":[OSD([sQuery(id+"F0.wireOp",EDGE,"E1.right")])]});
            var sketch = newSketch(context, id + "F26", { "sketchPlane" : qUnion([Q0])});
            skCircle(sketch, "E40", {"center": v(-34.56, 3) * mm, "radius": 0.25 * mm});
            skCircle(sketch, "E41", {"center": v(-11.83, 3) * mm, "radius": 0.25 * mm});
            skCircle(sketch, "E42", {"center": v(10.9, 3) * mm, "radius": 0.25 * mm});
            skCircle(sketch, "E43", {"center": v(33.63, 3) * mm, "radius": 0.25 * mm});
            skSolve(sketch);
        }
        {
            var Q0;
            {var subQ0=makeQuery(id+"F1.opExtrude","CAP_EDGE",EDGE,{"disambiguationData":[OSD([sQuery(id+"F0.wireOp",EDGE,"E1.right")])],"isStart":false});var subQ1=sQuery(id+"F26.wireOp",EDGE,"E40");var subQ3=makeQuery(id+"F26.imprint","INTERSECT",VERTEX,{"disambiguationData":[OD(0.0)],"derivedFrom":[subQ0,subQ1]});var subQ5=sQuery(id+"F26.wireOp",EDGE,"E41");var subQ7=makeQuery(id+"F26.imprint","INTERSECT",VERTEX,{"disambiguationData":[OD(0.0)],"derivedFrom":[subQ0,subQ5]});var subQ9=sQuery(id+"F26.wireOp",EDGE,"E42");var subQ11=makeQuery(id+"F26.imprint","INTERSECT",VERTEX,{"disambiguationData":[OD(0.0)],"derivedFrom":[subQ0,subQ9]});var subQ13=sQuery(id+"F26.wireOp",EDGE,"E43");var subQ15=makeQuery(id+"F26.imprint","INTERSECT",VERTEX,{"disambiguationData":[OD(0.0)],"derivedFrom":[subQ0,subQ13]});Q0=qUnion([makeQuery(id+"F26.imprint","IMPRINT",FACE,{"disambiguationData":[TD([[makeQuery(id+"F26.imprint","IMPRINT",EDGE,{"disambiguationData":[TD([[subQ3,1.0]])],"derivedFrom":subQ1}),1.0]])]}),makeQuery(id+"F26.imprint","IMPRINT",FACE,{"disambiguationData":[TD([[makeQuery(id+"F26.imprint","IMPRINT",EDGE,{"disambiguationData":[TD([[subQ7,1.0]])],"derivedFrom":subQ5}),1.0]])]}),makeQuery(id+"F26.imprint","IMPRINT",FACE,{"disambiguationData":[TD([[makeQuery(id+"F26.imprint","IMPRINT",EDGE,{"disambiguationData":[TD([[subQ11,-1.0]])],"derivedFrom":subQ9}),1.0]])]}),makeQuery(id+"F26.imprint","IMPRINT",FACE,{"disambiguationData":[TD([[makeQuery(id+"F26.imprint","IMPRINT",EDGE,{"disambiguationData":[TD([[subQ15,-1.0]])],"derivedFrom":subQ13}),1.0]])]}),makeQuery(id+"F26.imprint","IMPRINT",FACE,{"disambiguationData":[TD([[makeQuery(id+"F26.imprint","IMPRINT",EDGE,{"disambiguationData":[TD([[subQ3,-1.0]])],"derivedFrom":subQ1}),1.0]])]}),makeQuery(id+"F26.imprint","IMPRINT",FACE,{"disambiguationData":[TD([[makeQuery(id+"F26.imprint","IMPRINT",EDGE,{"disambiguationData":[TD([[subQ7,-1.0]])],"derivedFrom":subQ5}),1.0]])]}),makeQuery(id+"F26.imprint","IMPRINT",FACE,{"disambiguationData":[TD([[makeQuery(id+"F26.imprint","IMPRINT",EDGE,{"disambiguationData":[TD([[subQ11,1.0]])],"derivedFrom":subQ9}),1.0]])]}),makeQuery(id+"F26.imprint","IMPRINT",FACE,{"disambiguationData":[TD([[makeQuery(id+"F26.imprint","IMPRINT",EDGE,{"disambiguationData":[TD([[subQ15,1.0]])],"derivedFrom":subQ13}),1.0]])]})]);}
            extrude(context, id + "F27", {"entities" : qUnion([Q0]), "operationType" : NewBodyOperationType.REMOVE, "oppositeDirection" : true, "depth" : 7 * mm});
        }
        {
            var Q0;
            Q0 = qSketchRegion(id + "F22", true);
            extrude(context, id + "F28", {"entities" : qUnion([Q0]), "operationType" : NewBodyOperationType.REMOVE, "oppositeDirection" : true, "depth" : 4 * mm});
        }
    });
